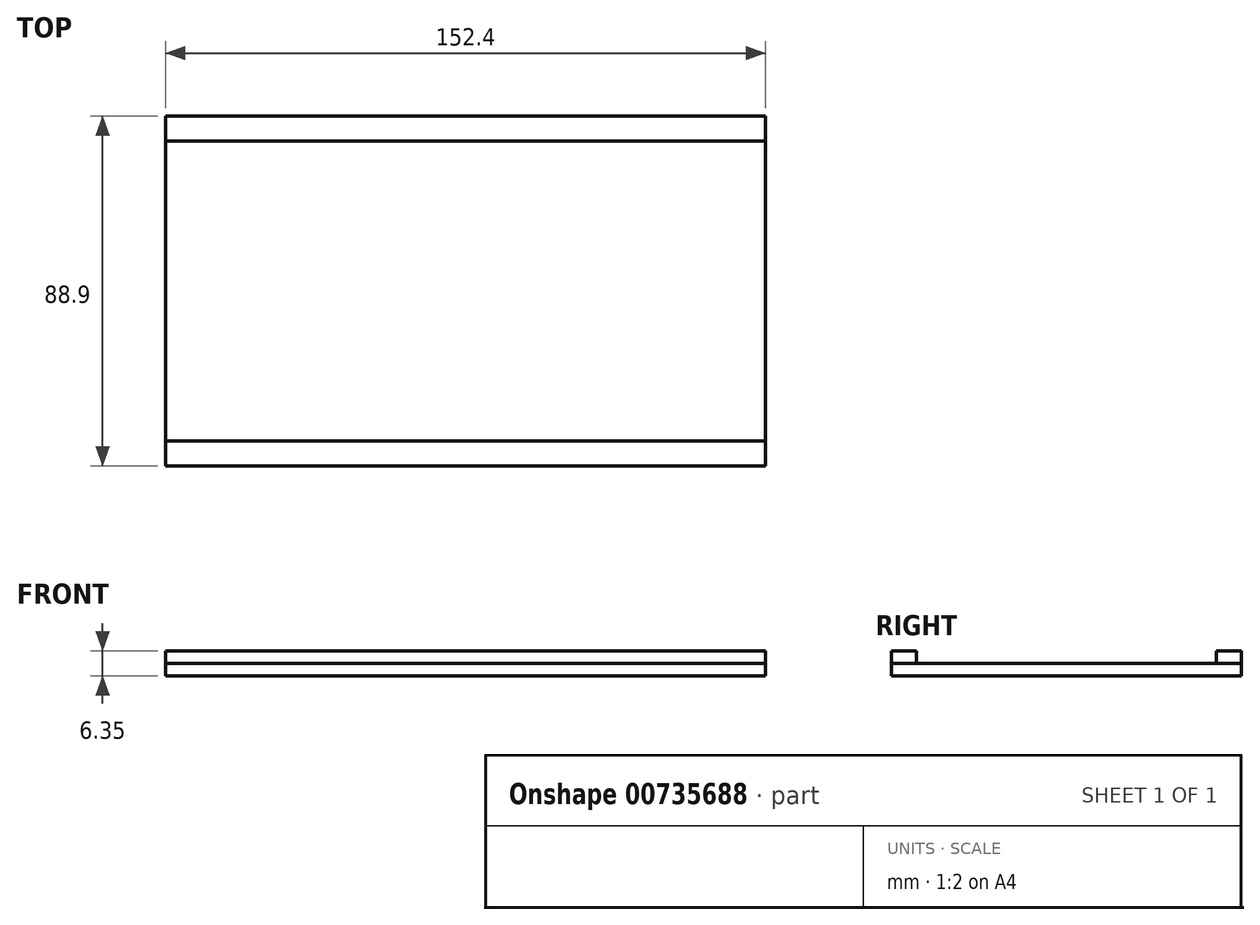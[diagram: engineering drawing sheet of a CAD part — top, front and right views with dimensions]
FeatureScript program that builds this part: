
annotation { "Feature Type Name" : "Feature", "Feature Type Description" : "" }
export const myFeature = defineFeature(function(context is Context, id is Id, definition is map)
    precondition{}
    {
        {
            var Q0;
            Q0=qCreatedBy(makeId("Top.planeOp"),FACE);
            var sketch = newSketch(context, id + "F0", { "sketchPlane" : qUnion([Q0])});
            skLineSegment(sketch, "E0.bottom", {"start": v(0, 0) * mm, "end": v(152.4, 0) * mm});
            skLineSegment(sketch, "E0.top", {"start": v(0, 88.9) * mm, "end": v(152.4, 88.9) * mm});
            skLineSegment(sketch, "E0.left", {"start": v(0, 0) * mm, "end": v(0, 88.9) * mm});
            skLineSegment(sketch, "E0.right", {"start": v(152.4, 0) * mm, "end": v(152.4, 88.9) * mm});
            skSolve(sketch);
        }
        {
            var Q0;
            Q0 = qSketchRegion(id + "F0", true);
            extrude(context, id + "F1", {"entities" : qUnion([Q0]), "depth" : 3.17 * mm, "offsetDistance" : 25.4 * mm});
        }
        {
            var Q0;
            Q0=makeQuery(id+"F1.opExtrude","CAP_FACE",FACE,{"disambiguationData":[OSD([sQuery(id+"F0.wireOp",EDGE,"E0.bottom"),sQuery(id+"F0.wireOp",EDGE,"E0.top"),sQuery(id+"F0.wireOp",EDGE,"E0.left"),sQuery(id+"F0.wireOp",EDGE,"E0.right")])],"isStart":false});
            var sketch = newSketch(context, id + "F2", { "sketchPlane" : qUnion([Q0])});
            skLineSegment(sketch, "E1.bottom", {"start": v(0, 0) * mm, "end": v(152.4, 0) * mm});
            skLineSegment(sketch, "E1.top", {"start": v(0, 6.35) * mm, "end": v(152.4, 6.35) * mm});
            skLineSegment(sketch, "E1.left", {"start": v(0, 0) * mm, "end": v(0, 6.35) * mm});
            skLineSegment(sketch, "E1.right", {"start": v(152.4, 0) * mm, "end": v(152.4, 6.35) * mm});
            skSolve(sketch);
        }
        {
            var Q0;
            {var subQ0=sQuery(id+"F2.wireOp",EDGE,"E1.top");Q0=makeQuery(id+"F2.imprint","IMPRINT",FACE,{"disambiguationData":[TD([[makeQuery(id+"F2.imprint","IMPRINT",EDGE,{"derivedFrom":subQ0}),1.0]])]});}
            var sketch = newSketch(context, id + "F3", { "sketchPlane" : qUnion([Q0])});
            skLineSegment(sketch, "E2", {"start": v(152.4, 82.55) * mm, "end": v(152.4, 88.9) * mm});
            skLineSegment(sketch, "E3", {"start": v(152.4, 82.55) * mm, "end": v(0, 82.55) * mm});
            skLineSegment(sketch, "E4", {"start": v(0, 82.55) * mm, "end": v(0, 88.87) * mm});
            skLineSegment(sketch, "E5", {"start": v(0, 88.87) * mm, "end": v(152.4, 88.9) * mm});
            skSolve(sketch);
        }
        {
            var Q0;
            Q0 = qSketchRegion(id + "F2", true);
            extrude(context, id + "F4", {"entities" : qUnion([Q0]), "depth" : 3.17 * mm, "offsetDistance" : 25.4 * mm});
        }
        {
            var Q0;
            Q0 = qSketchRegion(id + "F3", true);
            extrude(context, id + "F5", {"entities" : qUnion([Q0]), "depth" : 3.17 * mm, "offsetDistance" : 25.4 * mm});
        }
    });
